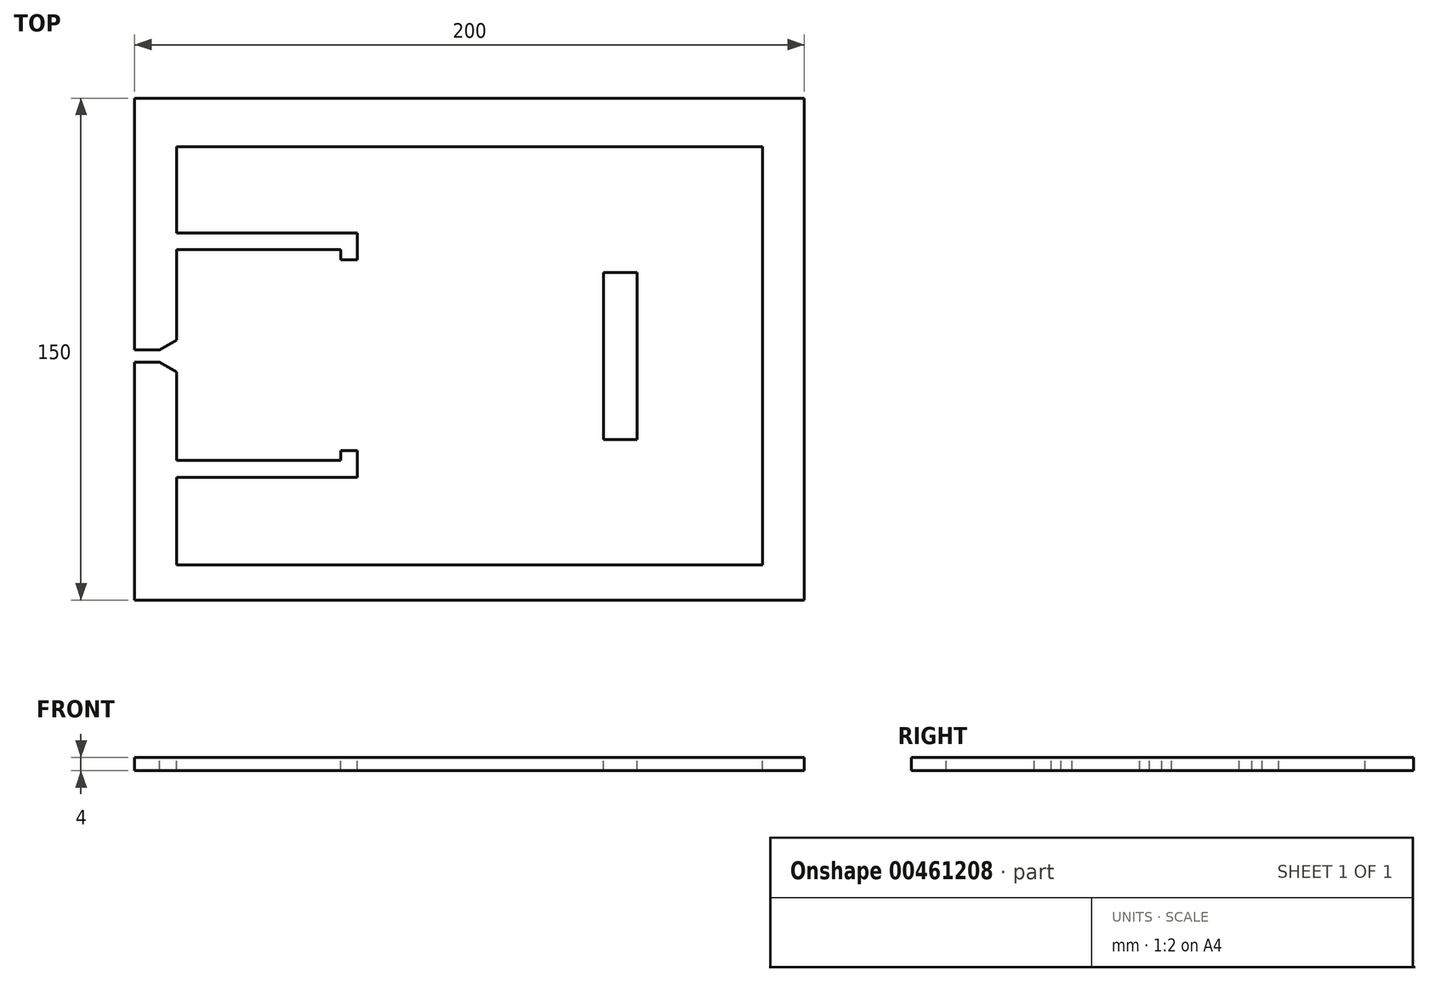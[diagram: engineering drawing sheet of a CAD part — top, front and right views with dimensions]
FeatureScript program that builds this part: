
annotation { "Feature Type Name" : "Feature", "Feature Type Description" : "" }
export const myFeature = defineFeature(function(context is Context, id is Id, definition is map)
    precondition{}
    {
        {
            var Q0;
            Q0=qCreatedBy(makeId("Top.planeOp"),FACE);
            var sketch = newSketch(context, id + "F0", { "sketchPlane" : qUnion([Q0])});
            skLineSegment(sketch, "E0.bottom", {"start": v(100, 75) * mm, "end": v(-100, 75) * mm});
            skLineSegment(sketch, "E0.top", {"start": v(100, -75) * mm, "end": v(-100, -75) * mm});
            skLineSegment(sketch, "E0.left", {"start": v(100, 75) * mm, "end": v(100, -75) * mm});
            skLineSegment(sketch, "E0.right", {"start": v(-100, 75) * mm, "end": v(-100, -75) * mm});
            skPoint(sketch, "E0.middle", {"position": v(0, 0) * mm});
            skSolve(sketch);
        }
        {
            var Q0;
            Q0=makeQuery(id+"F0.imprint","IMPRINT",FACE,{"disambiguationData":[TD([[makeQuery(id+"F0.imprint","IMPRINT",EDGE,{"derivedFrom":sQuery(id+"F0.wireOp",EDGE,"E0.bottom")}),1.0]])]});
            extrude(context, id + "F1", {"entities" : qUnion([Q0]), "depth" : 4 * mm, "offsetDistance" : 25 * mm});
        }
        {
            var Q0;
            Q0=makeQuery(id+"F1.opExtrude","CAP_FACE",FACE,{"disambiguationData":[OSD([sQuery(id+"F0.wireOp",EDGE,"E0.bottom"),sQuery(id+"F0.wireOp",EDGE,"E0.top"),sQuery(id+"F0.wireOp",EDGE,"E0.left"),sQuery(id+"F0.wireOp",EDGE,"E0.right")])],"isStart":false});
            var sketch = newSketch(context, id + "F2", { "sketchPlane" : qUnion([Q0])});
            skLineSegment(sketch, "E1.bottom", {"start": v(87.5, 60.44) * mm, "end": v(-87.5, 60.44) * mm});
            skLineSegment(sketch, "E1.top", {"start": v(87.5, -64.56) * mm, "end": v(-77.5, -64.56) * mm});
            skLineSegment(sketch, "E1.left", {"start": v(87.5, 60.44) * mm, "end": v(87.5, -64.56) * mm});
            skLineSegment(sketch, "E1.right", {"start": v(-87.5, 60.44) * mm, "end": v(-87.5, 34.72) * mm});
            skPoint(sketch, "E1.middle", {"position": v(0, -2.06) * mm});
            skLineSegment(sketch, "E2.bottom", {"start": v(-87.5, 29.72) * mm, "end": v(-46, 29.72) * mm});
            skLineSegment(sketch, "E3", {"start": v(-46, -38.28) * mm, "end": v(-87.5, -38.28) * mm});
            skLineSegment(sketch, "E4", {"start": v(-41, -38.28) * mm, "end": v(-46, -38.28) * mm});
            skLineSegment(sketch, "E5", {"start": v(-41, 34.72) * mm, "end": v(-87.5, 34.72) * mm});
            skLineSegment(sketch, "E6.trimOffspring", {"start": v(-87.5, -38.28) * mm, "end": v(-87.5, -64.56) * mm});
            skLineSegment(sketch, "E7", {"start": v(-6, -30.28) * mm, "end": v(-6, 26.72) * mm});
            skLineSegment(sketch, "E8", {"start": v(-74.36, 50.44) * mm, "end": v(60.64, 50.44) * mm});
            skLineSegment(sketch, "E9", {"start": v(60.64, 47.44) * mm, "end": v(-74.36, 47.44) * mm});
            skLineSegment(sketch, "E10", {"start": v(-74.36, 50.44) * mm, "end": v(-77.36, 50.44) * mm});
            skLineSegment(sketch, "E11", {"start": v(-77.36, 50.44) * mm, "end": v(-77.36, 47.44) * mm});
            skLineSegment(sketch, "E12", {"start": v(-77.36, 47.44) * mm, "end": v(-74.36, 47.44) * mm});
            skLineSegment(sketch, "E13", {"start": v(-87.5, -64.56) * mm, "end": v(-77.5, -64.56) * mm});
            skLineSegment(sketch, "E14", {"start": v(-77.5, -54.56) * mm, "end": v(60.64, -54.56) * mm});
            skLineSegment(sketch, "E15", {"start": v(60.64, -51.56) * mm, "end": v(-77.5, -51.56) * mm});
            skLineSegment(sketch, "E16", {"start": v(-77.5, -54.56) * mm, "end": v(-77.5, -51.56) * mm});
            skLineSegment(sketch, "E17", {"start": v(60.64, 47.44) * mm, "end": v(57.64, 47.44) * mm});
            skLineSegment(sketch, "E18", {"start": v(60.64, 50.44) * mm, "end": v(77.5, 50.44) * mm});
            skLineSegment(sketch, "E19", {"start": v(77.5, 50.44) * mm, "end": v(77.5, -54.56) * mm});
            skLineSegment(sketch, "E20", {"start": v(77.5, -54.56) * mm, "end": v(60.64, -54.56) * mm});
            skLineSegment(sketch, "E21", {"start": v(77.5, 50.44) * mm, "end": v(77.5, 47.44) * mm});
            skLineSegment(sketch, "E22", {"start": v(69.5, 47.44) * mm, "end": v(60.64, 47.44) * mm});
            skLineSegment(sketch, "E23", {"start": v(77.5, 50.44) * mm, "end": v(74.5, 50.44) * mm});
            skLineSegment(sketch, "E24", {"start": v(74.5, 42.44) * mm, "end": v(74.5, -46.56) * mm});
            skLineSegment(sketch, "E25", {"start": v(60.64, -51.56) * mm, "end": v(69.5, -51.56) * mm});
            skPoint(sketch, "E26.end.orphan", {"position": v(77.5, 48.67) * mm});
            skArc(sketch, "E27.filletArc", {"start": v(74.5, 42.44) * mm, "mid": v(73.03, 45.97) * mm, "end": v(69.5, 47.44) * mm});
            skPoint(sketch, "E28.visualSharp", {"position": v(74.5, -51.56) * mm});
            skArc(sketch, "E28.filletArc", {"start": v(69.5, -51.56) * mm, "mid": v(73.03, -50.1) * mm, "end": v(74.5, -46.56) * mm});
            skLineSegment(sketch, "E29", {"start": v(-87.5, 29.72) * mm, "end": v(-38.5, 29.72) * mm});
            skLineSegment(sketch, "E30", {"start": v(-38.5, 29.72) * mm, "end": v(-38.5, 26.72) * mm});
            skLineSegment(sketch, "E31", {"start": v(-38.5, 26.72) * mm, "end": v(-33.5, 26.72) * mm});
            skLineSegment(sketch, "E32", {"start": v(-33.5, 26.72) * mm, "end": v(-33.5, 34.72) * mm});
            skLineSegment(sketch, "E33", {"start": v(-33.5, 34.72) * mm, "end": v(-41, 34.72) * mm});
            skLineSegment(sketch, "E34", {"start": v(-100, -0.26) * mm, "end": v(-100, -3.86) * mm});
            skLineSegment(sketch, "E35", {"start": v(-100, -0.26) * mm, "end": v(-92.5, -0.26) * mm});
            skLineSegment(sketch, "E36", {"start": v(-100, -3.86) * mm, "end": v(-92.5, -3.86) * mm});
            skLineSegment(sketch, "E37", {"start": v(-87.5, -6.86) * mm, "end": v(-92.5, -3.86) * mm});
            skLineSegment(sketch, "E38", {"start": v(-92.5, -0.26) * mm, "end": v(-87.5, 2.74) * mm});
            skLineSegment(sketch, "E39", {"start": v(-87.5, 2.74) * mm, "end": v(-87.5, 29.72) * mm});
            skLineSegment(sketch, "E40", {"start": v(-87.5, -6.86) * mm, "end": v(-87.5, -33.28) * mm});
            skLineSegment(sketch, "E41", {"start": v(-87.5, -33.28) * mm, "end": v(-38.5, -33.28) * mm});
            skLineSegment(sketch, "E42", {"start": v(-38.5, -33.28) * mm, "end": v(-38.5, -30.28) * mm});
            skLineSegment(sketch, "E43", {"start": v(-38.5, -30.28) * mm, "end": v(-33.5, -30.28) * mm});
            skLineSegment(sketch, "E44", {"start": v(-33.5, -30.28) * mm, "end": v(-33.5, -38.28) * mm});
            skLineSegment(sketch, "E45", {"start": v(-33.5, -38.28) * mm, "end": v(-41, -38.28) * mm});
            skPoint(sketch, "E46.start.orphan", {"position": v(-41, -30.28) * mm});
            skLineSegment(sketch, "E47", {"start": v(0, -2.06) * mm, "end": v(40, -2.06) * mm});
            skLineSegment(sketch, "E48", {"start": v(40, -2.06) * mm, "end": v(40, 35.44) * mm});
            skLineSegment(sketch, "E49", {"start": v(40, -2.06) * mm, "end": v(40, -39.56) * mm});
            skPoint(sketch, "E50.end.orphan", {"position": v(42.97, -39.56) * mm});
            skLineSegment(sketch, "E51", {"start": v(40, 35.44) * mm, "end": v(50, 35.44) * mm});
            skLineSegment(sketch, "E52", {"start": v(50, 35.44) * mm, "end": v(50, -39.56) * mm});
            skLineSegment(sketch, "E53", {"start": v(50, -39.56) * mm, "end": v(40, -39.56) * mm});
            skLineSegment(sketch, "E54", {"start": v(40, -2.06) * mm, "end": v(40, 22.94) * mm});
            skLineSegment(sketch, "E55", {"start": v(40, 22.94) * mm, "end": v(50, 22.94) * mm});
            skLineSegment(sketch, "E56", {"start": v(40, -2.06) * mm, "end": v(40, -27.06) * mm});
            skLineSegment(sketch, "E57", {"start": v(40, -27.06) * mm, "end": v(50, -27.06) * mm});
            skSolve(sketch);
        }
        {
            var Q0;
            Q0=makeQuery(id+"F2.imprint","IMPRINT",FACE,{"disambiguationData":[TD([[makeQuery(id+"F2.imprint","IMPRINT",EDGE,{"derivedFrom":sQuery(id+"F2.wireOp",EDGE,"E1.bottom")}),1.0]])]});
            var Q1;
            Q1=makeQuery(id+"F2.imprint","IMPRINT",FACE,{"disambiguationData":[TD([[makeQuery(id+"F2.imprint","IMPRINT",EDGE,{"derivedFrom":sQuery(id+"F2.wireOp",EDGE,"E8")}),-1.0]])]});
            var Q2;
            Q2=makeQuery(id+"F2.imprint","IMPRINT",FACE,{"disambiguationData":[TD([[makeQuery(id+"F2.imprint","IMPRINT",EDGE,{"derivedFrom":sQuery(id+"F2.wireOp",EDGE,"E48")}),-1.0]])]});
            var Q3;
            Q3=makeQuery(id+"F2.imprint","IMPRINT",FACE,{"disambiguationData":[TD([[makeQuery(id+"F2.imprint","IMPRINT",EDGE,{"derivedFrom":sQuery(id+"F2.wireOp",EDGE,"E54")}),-1.0]])]});
            var Q4;
            Q4=makeQuery(id+"F2.imprint","IMPRINT",FACE,{"disambiguationData":[TD([[makeQuery(id+"F2.imprint","IMPRINT",EDGE,{"derivedFrom":sQuery(id+"F2.wireOp",EDGE,"E49")}),1.0]])]});
            extrude(context, id + "F3", {"entities" : qUnion([Q0, Q1, Q2, Q3, Q4]), "operationType" : NewBodyOperationType.REMOVE, "oppositeDirection" : true, "depth" : 25 * mm, "offsetDistance" : 25 * mm});
        }
    });
